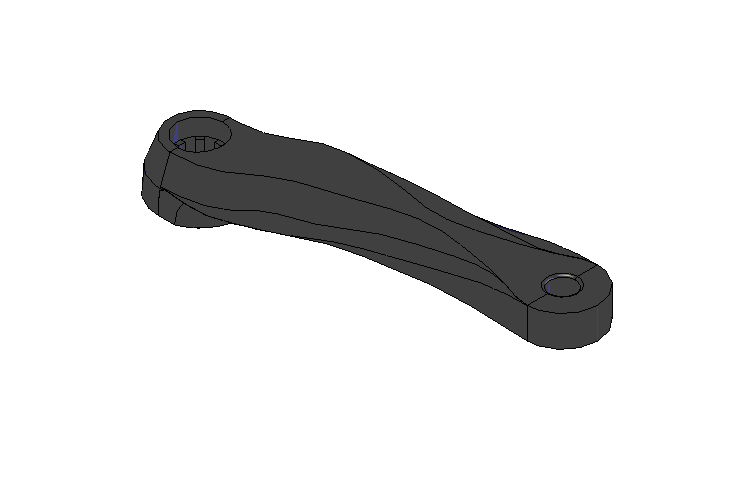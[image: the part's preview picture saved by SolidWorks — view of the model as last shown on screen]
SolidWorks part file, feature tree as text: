
SOLIDWORKS PART (.sldprt)
format: sldprt  version: not decoded by parser v0  size: 1,525,760 bytes
history: native  units: mm
features: sketch x32, plane x16, revolve x2, fillet x2, cut_extrude x2, material x1, sweep x1, cut_revolve x1, pattern_circular x1 (+10 scaffold rows collapsed)
feature tree (68):
  scaffold x10  (default folders/planes/origin — collapsed)
  material  "Matériau <non spécifié>"
  plane  "Plan de face"
  plane  "Plan de dessus"
  plane  "Plan de droite"
  plane  "Plan0"  Offset=0mm
  plane  "Plan17"  Offset=17mm
  plane  "Plan34"  Offset=34mm
  plane  "Plan51"  Offset=51mm
  plane  "Plan68"  Offset=68mm
  plane  "Plan85"  Offset=85mm
  plane  "Plan102"  Offset=102mm
  plane  "Plan119"  Offset=119mm
  plane  "Plan136"  Offset=136mm
  plane  "Plan153"  Offset=153mm
  plane  "Plan170"  Offset=170mm
  sketch  "Esquisse1"  dims[D1=30.0mm D2=32.0mm D3=38.0mm D4=44.0mm D5=47.0mm D6=49.0mm D7=50.0mm D8=51.0mm D9=52.0mm D10=53.0mm D11=54.0mm]
  sketch  "Esquisse2"  dims[D1=18.0mm D2=18.0mm D3=22.0mm D4=27.0mm D5=32.0mm D6=36.0mm D7=38.0mm D8=39.5mm D9=40.5mm D10=40.0mm D11=39.5mm]
  sketch  "Esquisse3"  dims[c1.D1=37.0mm c1.D2=42.0mm c1.D3=42.0mm c1.D4=42.0mm c1.D5=40.0mm c1.D6=38.0mm c1.D7=36.0mm c1.D8=34.0mm c1.D9=33.0mm c1.D10=33.0mm c1.D11=33.0mm c2.D2=39.5mm]
  sketch  "Esquisse4"  dims[D1=28.0mm D2=28.0mm D3=28.0mm D4=25.0mm D5=21.0mm D6=15.0mm D7=7.0mm D8=7.0mm D9=14.0mm D10=23.0mm D11=33.0mm D12=~178.970178mm]
  sketch  "Esquisse5"
  sketch  "Esquisse6"  dims[D1=11.0mm D2=11.0mm D3=9.0mm D4=8.0mm D5=6.0mm D6=1.5mm D7=3.0mm D8=2.0mm]
  sketch  "Esquisse7"  dims[D1=35.0mm D2=28.0mm D3=24.0mm D4=21.0mm D5=~14.673184mm]
  sketch  "Esquisse8"  dims[D1=0.0mm]
  sketch  "Esquisse9"  dims[D1=11.0mm]
  sketch  "Esquisse10"  dims[c1.D1=5.0mm c1.D2=0.1mm c2.D1=0.1mm]
  sketch  "Esquisse11"  dims[D1=0.1mm]
  sketch  "Esquisse12"  dims[D1=0.1mm]
  sketch  "Esquisse13"  dims[D1=0.1mm]
  sketch  "Esquisse14"  dims[D1=0.1mm]
  sketch  "Esquisse15"
  sketch  "Esquisse16"
  sketch  "Esquisse17"
  sketch  "Esquisse18"
  sketch  "Esquisse19"  dims[c1.D1=2.0mm c1.D2=~12.895463mm c2.D1=0.1mm]
  sketch  "Esquisse20"  dims[c1.D1=0.1mm c1.D2=0.1mm c2.D1=~2.574604mm c2.D2=3.0mm c3.D1=0.1mm c3.D2=0.1mm]
  sketch  "Esquisse23"  dims[c1.D1=95.0mm c1.D2=1.5mm c1.D3=8.0mm c2.D2=1.5mm c2.D4=142.0mm c2.D5=10.0mm c3.D2=30.0mm c3.D6=2.0mm c3.D7=50.0mm c3.D8=~8.48585mm c4.D2=30.0mm c4.D7=8.0mm]
  sketch  "Esquisse24"  dims[c1.D2=~30.618801mm c1.D3=30.0mm c1.D1=~12.058422mm c2.D1=90.0deg c2.D2=15.0mm c2.D4=~15.479283mm]
  sweep  "Enlèvement de matière-Balayage2"
  sketch  "Esquisse21"
  revolve  "Révolution1"  Angle=180deg
  sketch  "Esquisse22"  dims[c1.D1=12.5mm c1.D2=38.0mm c2.D1=12.5mm c2.D2=10.0mm c2.D3=39.0mm c3.D2=23.0mm c3.D4=28.0mm c4.D2=23.0mm c4.D5=28.0mm c4.D6=37.0mm]
  revolve  "Révolution2"  Angle=360deg
  plane  "Plan171"  Offset=30mm
  plane  "Plan172"  Offset=17.5mm
  sketch  "Esquisse32"  dims[D1=21.0mm]
  sketch  "Esquisse33"  dims[D1=48.0mm]
  sketch  "Esquisse34"
  sketch  "Esquisse35"
  fillet  "Congé3"  Radius=3mm
  sketch  "Esquisse36"  dims[D1=12.0mm]
  sketch  "Esquisse38"  dims[D1=12.0mm]
  cut_extrude  "Enlèv. mat.-Extru.4"  [1 undecoded]
  fillet  "Congé4"  Radius=1mm
  sketch  "Esquisse39"  dims[c1.D1=21.5mm c1.D2=17.5mm c1.D3=21.6mm c1.D4=21.8mm c1.D5=10.0mm c2.D3=10.0005mm c3.D3=1.0deg c3.D6=20.0mm c3.D1=21.8mm c3.D2=~10.001523mm c4.D2=1.0deg c4.D3=10.0mm c4.D4=20.0mm c4.D5=17.5mm c4.D6=21.0mm c5.D2=17.0mm c5.D5=~10.001523mm c6.D5=1.0deg]
  cut_revolve  "Enlèvement de matière-Révolution1"  Angle=360deg
  sketch  "Esquisse40"  dims[c1.D2=21.6mm c1.D1=3.0mm c1.D3=~17.315298mm c2.D3=45.0deg c3.D3=~17.315298mm c4.D3=45.0deg c4.D1=~2.328726mm c5.D1=45.0deg c6.D1=~2.328726mm c7.D1=45.0deg c8.D1=~2.328726mm c9.D1=45.0deg c9.D2=~17.315298mm c10.D2=22.5deg c10.D3=~1.646658mm c10.D1=~2.328726mm c11.D1=45.0deg c11.D3=~3.63188mm]
  cut_extrude  "Enlèv. mat.-Extru.5"  [1 undecoded]
  pattern_circular  "Répétition circulaire1"  Count=8 Angle=45deg
decode coverage: 30 of 41 modeling features carry decoded parameters
note: ~ marks probable driven/reference dimensions
note: 2 parameter values undecoded
note: suppression state not decoded; provenance and decode notes live in map.json
